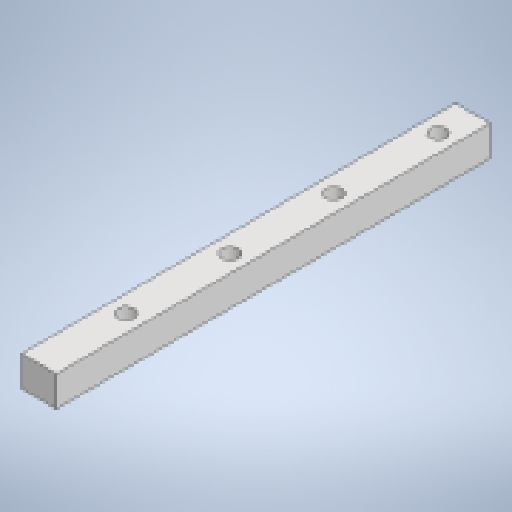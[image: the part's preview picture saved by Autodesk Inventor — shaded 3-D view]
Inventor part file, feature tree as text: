
AUTODESK INVENTOR PART (.ipt)
format: ipt  version: 2023 (Build 270158000, 158)  size: 155,648 bytes
history: native  units: mm
features: extrude x3, sketch x3, pattern_linear x1
ambient origin geometry x8: Origin, YZ Plane, XZ Plane, XY Plane, X Axis, Y Axis, Z Axis, Center Point
bodies: Solid1 (feature_tree)
feature tree (7):
  extrude  "Extrusion1"  Depth=17.5mm
  extrude  "Extrusion2"  Depth=250.0mm
  extrude  "Extrusion3"  Depth=8.5mm TaperAngle=0.0deg
  pattern_linear  "Rectangular Pattern1"  Spacing1=9.5mm  [1 undecoded]
  sketch  "Sketch1"  dims[d0=20.0mm d1=17.5mm]
  sketch  "Sketch2"  dims[d2=250.0mm d3=0.0mm d4=6.0mm]
  sketch  "Sketch3"  dims[d5=20.0mm d6=800.0mm d7=0.0mm d8=9.5mm d9=8.5mm d10=0.0mm d11=180.0mm d13=60.0mm]
note: 1 required parameter value undecoded (feature->parameter linkage not recoverable at this tier; creation-order binding heuristic only, values carry confidence <= 0.55)
